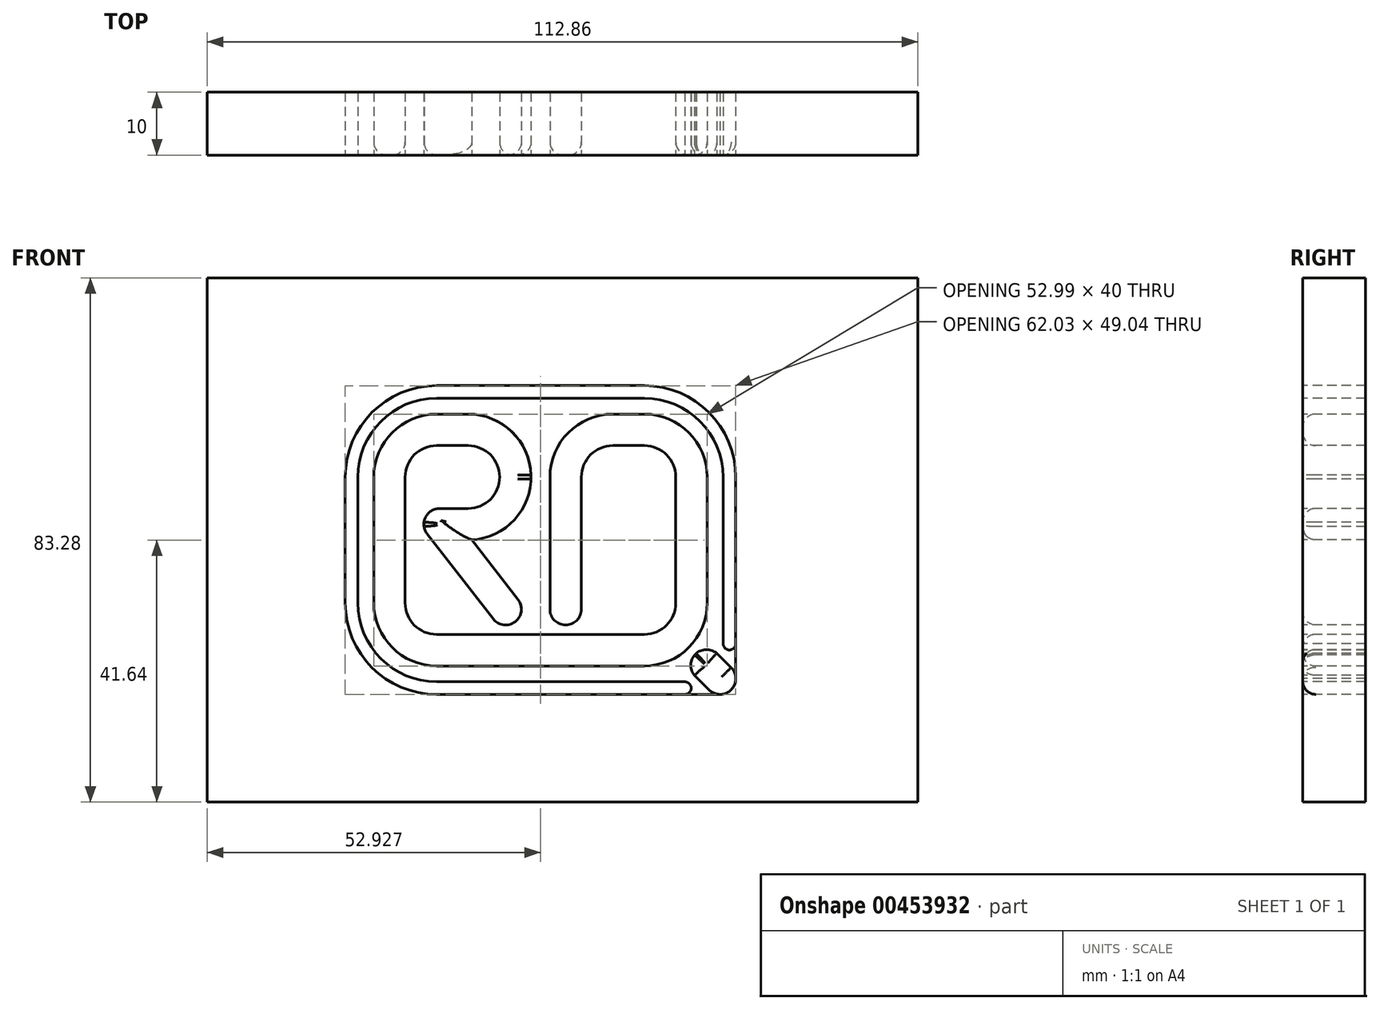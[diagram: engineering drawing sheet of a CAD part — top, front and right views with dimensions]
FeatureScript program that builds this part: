
annotation { "Feature Type Name" : "Feature", "Feature Type Description" : "" }
export const myFeature = defineFeature(function(context is Context, id is Id, definition is map)
    precondition{}
    {
        {
            var Q0;
            Q0=qCreatedBy(makeId("Front.planeOp"),FACE);
            var sketch = newSketch(context, id + "F0", { "sketchPlane" : qUnion([Q0])});
            skPoint(sketch, "E0.middle", {"position": v(0, 0) * mm});
            skLineSegment(sketch, "E1", {"start": v(-25, 10) * mm, "end": v(-25, -10) * mm});
            skLineSegment(sketch, "E2", {"start": v(-2, -20) * mm, "end": v(-0.38, -20) * mm});
            skLineSegment(sketch, "E3", {"start": v(-2, -11) * mm, "end": v(-2, 10) * mm});
            skLineSegment(sketch, "E4", {"start": v(8, 20) * mm, "end": v(13, 20) * mm});
            skLineSegment(sketch, "E5", {"start": v(23, 10) * mm, "end": v(23, -10) * mm});
            skLineSegment(sketch, "E6", {"start": v(13, -20) * mm, "end": v(9, -20) * mm});
            skLineSegment(sketch, "E7", {"start": v(-25, 20) * mm, "end": v(-15, 20) * mm});
            skLineSegment(sketch, "E8", {"start": v(-21, 0) * mm, "end": v(-15, 0) * mm, "construction": true});
            skLineSegment(sketch, "E9", {"start": v(-5, 10.33) * mm, "end": v(-5, 10.33) * mm});
            skPoint(sketch, "E10.visualSharp", {"position": v(-5.33, 20) * mm});
            skArc(sketch, "E10.filletArc", {"start": v(-5, 10.33) * mm, "mid": v(-8.05, 17.19) * mm, "end": v(-15, 20) * mm});
            skArc(sketch, "E11.filletArc", {"start": v(-15, 0) * mm, "mid": v(-7.81, 3.05) * mm, "end": v(-5, 10.33) * mm});
            skPoint(sketch, "E12.visualSharp", {"position": v(-3.63, -20) * mm});
            skPoint(sketch, "E13.visualSharp", {"position": v(23, -20) * mm});
            skArc(sketch, "E13.filletArc", {"start": v(13, -20) * mm, "mid": v(20.07, -17.07) * mm, "end": v(23, -10) * mm});
            skPoint(sketch, "E14.visualSharp", {"position": v(23, 20) * mm});
            skArc(sketch, "E14.filletArc", {"start": v(23, 10) * mm, "mid": v(20.07, 17.07) * mm, "end": v(13, 20) * mm});
            skPoint(sketch, "E15.visualSharp", {"position": v(-2, 20) * mm});
            skArc(sketch, "E15.filletArc", {"start": v(8, 20) * mm, "mid": v(0.92, 17.07) * mm, "end": v(-2, 10) * mm});
            skPoint(sketch, "E16.visualSharp", {"position": v(-2, -20) * mm});
            skArc(sketch, "E17.0", {"start": v(8, 15) * mm, "mid": v(4.46, 13.54) * mm, "end": v(3, 10) * mm});
            skLineSegment(sketch, "E17.1", {"start": v(3, -11) * mm, "end": v(3, 10) * mm});
            skLineSegment(sketch, "E17.2", {"start": v(8, 15) * mm, "end": v(13, 15) * mm});
            skArc(sketch, "E17.4", {"start": v(18, 10) * mm, "mid": v(16.53, 13.54) * mm, "end": v(13, 15) * mm});
            skLineSegment(sketch, "E17.5", {"start": v(18, 10) * mm, "end": v(18, -10) * mm});
            skArc(sketch, "E17.6", {"start": v(13, -15) * mm, "mid": v(16.53, -13.54) * mm, "end": v(18, -10) * mm});
            skLineSegment(sketch, "E17.7", {"start": v(13, -15) * mm, "end": v(9, -15) * mm});
            skArc(sketch, "E18.1", {"start": v(-15, 5) * mm, "mid": v(-11.44, 6.5) * mm, "end": v(-10, 10.08) * mm});
            skArc(sketch, "E18.2", {"start": v(-10, 10.08) * mm, "mid": v(-11.5, 13.56) * mm, "end": v(-15, 15) * mm});
            skLineSegment(sketch, "E18.3", {"start": v(-20, 15) * mm, "end": v(-15, 15) * mm});
            skLineSegment(sketch, "E19.0", {"start": v(-30, 17.5) * mm, "end": v(-30, -10) * mm});
            skLineSegment(sketch, "E20.0", {"start": v(-1, -15) * mm, "end": v(-0.38, -15) * mm});
            skLineSegment(sketch, "E21", {"start": v(-20, -20) * mm, "end": v(-2, -20) * mm});
            skLineSegment(sketch, "E22", {"start": v(-1, -15) * mm, "end": v(9, -15) * mm});
            skLineSegment(sketch, "E23.0", {"start": v(-20, -15) * mm, "end": v(0, -15) * mm});
            skLineSegment(sketch, "E24", {"start": v(-5, 10.33) * mm, "end": v(-5, 0) * mm});
            skLineSegment(sketch, "E25", {"start": v(0.5, -13.5) * mm, "end": v(0.5, -13.5) * mm});
            skPoint(sketch, "E26.visualSharp", {"position": v(3, -13.5) * mm});
            skArc(sketch, "E26.filletArc", {"start": v(0.5, -13.5) * mm, "mid": v(2.26, -12.77) * mm, "end": v(3, -11) * mm});
            skPoint(sketch, "E27.newPointB", {"position": v(-23.5, -13.5) * mm});
            skArc(sketch, "E27.filletArc", {"start": v(-2, -11) * mm, "mid": v(-1.27, -12.77) * mm, "end": v(0.5, -13.5) * mm});
            skPoint(sketch, "E28.visualSharp", {"position": v(-30, -20) * mm});
            skArc(sketch, "E28.filletArc", {"start": v(-30, -19.5) * mm, "mid": v(-29.85, -19.85) * mm, "end": v(-29.5, -20) * mm});
            skLineSegment(sketch, "E29", {"start": v(-7.28, -12.77) * mm, "end": v(-7.28, -12.77) * mm});
            skArc(sketch, "E30.filletArc", {"start": v(-7.28, -12.77) * mm, "mid": v(-6.55, -11) * mm, "end": v(-7.27, -9.24) * mm});
            skArc(sketch, "E31.filletArc", {"start": v(-11.23, -12.21) * mm, "mid": v(-9.4, -13.48) * mm, "end": v(-7.28, -12.77) * mm});
            skLineSegment(sketch, "E32.0", {"start": v(19.16, -19.7) * mm, "end": v(23.25, -23.79) * mm});
            skLineSegment(sketch, "E33.0", {"start": v(14.76, -15.3) * mm, "end": v(14.29, -14.83) * mm});
            skPoint(sketch, "E34.newPointB", {"position": v(-25, 20) * mm});
            skPoint(sketch, "E35.visualSharp", {"position": v(-23.5, 5) * mm});
            skPoint(sketch, "E36.visualSharp", {"position": v(-23.5, 0) * mm});
            skLineSegment(sketch, "E37", {"start": v(-30, 10) * mm, "end": v(-30, 17.5) * mm});
            skLineSegment(sketch, "E38", {"start": v(-20, 20) * mm, "end": v(-25, 20) * mm});
            skPoint(sketch, "E39.visualSharp", {"position": v(-30, 20) * mm});
            skArc(sketch, "E39.filletArc", {"start": v(-20, 20) * mm, "mid": v(-27.07, 17.07) * mm, "end": v(-30, 10) * mm});
            skArc(sketch, "E40", {"start": v(23.25, -23.79) * mm, "mid": v(26.79, -23.79) * mm, "end": v(26.78, -20.25) * mm});
            skPoint(sketch, "E41", {"position": v(20.07, -17.07) * mm});
            skPoint(sketch, "E42.orphan", {"position": v(16.53, -13.54) * mm});
            skLineSegment(sketch, "E43.trimOffspring", {"start": v(13, -20) * mm, "end": v(-0.38, -20) * mm});
            skArc(sketch, "E44.trimOffspring", {"start": v(19.16, -19.7) * mm, "mid": v(21.12, -18.14) * mm, "end": v(22.69, -16.19) * mm});
            skPoint(sketch, "E45.newPointB", {"position": v(-25, -20) * mm});
            skArc(sketch, "E45.filletArc", {"start": v(-25, -10) * mm, "mid": v(-23.54, -13.54) * mm, "end": v(-20, -15) * mm});
            skLineSegment(sketch, "E46", {"start": v(-15, 20) * mm, "end": v(8, 20) * mm});
            skLineSegment(sketch, "E47", {"start": v(21.86, -24.52) * mm, "end": v(-20, -24.52) * mm});
            skLineSegment(sketch, "E48", {"start": v(27.51, -22.02) * mm, "end": v(27.51, -18.87) * mm});
            skLineSegment(sketch, "E49", {"start": v(13, 24.52) * mm, "end": v(-20, 24.52) * mm});
            skLineSegment(sketch, "E50", {"start": v(-34.52, -10) * mm, "end": v(-34.52, 10) * mm});
            skPoint(sketch, "E51.orphan", {"position": v(17.43, -17.97) * mm});
            skPoint(sketch, "E52.orphan", {"position": v(13.35, -13.89) * mm});
            skArc(sketch, "E53.0", {"start": v(27.51, 10) * mm, "mid": v(23.26, 20.27) * mm, "end": v(13, 24.52) * mm});
            skArc(sketch, "E54.0", {"start": v(25.51, 10) * mm, "mid": v(21.85, 18.85) * mm, "end": v(13, 22.52) * mm});
            skLineSegment(sketch, "E55.0", {"start": v(25.51, -22.07) * mm, "end": v(25.51, -19) * mm});
            skLineSegment(sketch, "E56.0", {"start": v(25.02, -22.52) * mm, "end": v(21.98, -22.52) * mm});
            skLineSegment(sketch, "E57.0", {"start": v(-32.52, -10) * mm, "end": v(-32.52, 10) * mm});
            skLineSegment(sketch, "E58.0", {"start": v(13, 22.52) * mm, "end": v(-20, 22.52) * mm});
            skPoint(sketch, "E59.visualSharp", {"position": v(-32.52, 22.52) * mm});
            skArc(sketch, "E59.filletArc", {"start": v(-20, 22.52) * mm, "mid": v(-28.85, 18.85) * mm, "end": v(-32.52, 10) * mm});
            skArc(sketch, "E60.0", {"start": v(-20, 24.52) * mm, "mid": v(-30.27, 20.27) * mm, "end": v(-34.52, 10) * mm});
            skPoint(sketch, "E61.visualSharp", {"position": v(-32.52, -22.52) * mm});
            skLineSegment(sketch, "E62", {"start": v(26.51, -15) * mm, "end": v(26.51, -16.32) * mm});
            skLineSegment(sketch, "E63.0", {"start": v(18.1, -20.77) * mm, "end": v(22.19, -24.85) * mm, "construction": true});
            skLineSegment(sketch, "E64.0", {"start": v(23.75, -15.12) * mm, "end": v(27.84, -19.2) * mm, "construction": true});
            skArc(sketch, "E65", {"start": v(19.44, -24.52) * mm, "mid": v(20.44, -23.52) * mm, "end": v(19.44, -22.52) * mm});
            skArc(sketch, "E66", {"start": v(25.51, -16.47) * mm, "mid": v(26.51, -17.47) * mm, "end": v(27.51, -16.47) * mm});
            skLineSegment(sketch, "E67.trimOffspring", {"start": v(25.51, -14) * mm, "end": v(25.51, 10) * mm});
            skLineSegment(sketch, "E68.trimOffspring", {"start": v(27.51, -14) * mm, "end": v(27.51, 33) * mm});
            skLineSegment(sketch, "E69.trimOffspring", {"start": v(19.86, -22.52) * mm, "end": v(-20, -22.52) * mm});
            skLineSegment(sketch, "E70", {"start": v(21.86, -24.52) * mm, "end": v(25.02, -24.52) * mm});
            skLineSegment(sketch, "E71", {"start": v(27.51, -14) * mm, "end": v(27.51, -22.02) * mm});
            skLineSegment(sketch, "E72.bottom", {"start": v(-56.43, 41.64) * mm, "end": v(56.43, 41.64) * mm});
            skLineSegment(sketch, "E72.top", {"start": v(-56.43, -41.64) * mm, "end": v(56.43, -41.64) * mm});
            skLineSegment(sketch, "E72.left", {"start": v(-56.43, 41.64) * mm, "end": v(-56.43, -41.64) * mm});
            skLineSegment(sketch, "E72.right", {"start": v(56.43, 41.64) * mm, "end": v(56.43, -41.64) * mm});
            skLineSegment(sketch, "E73", {"start": v(0, 0) * mm, "end": v(0, -38.7) * mm, "construction": true});
            skLineSegment(sketch, "E74", {"start": v(0, 0) * mm, "end": v(33.56, 0) * mm, "construction": true});
            skArc(sketch, "E75.filletArc", {"start": v(-20, 15) * mm, "mid": v(-23.54, 13.54) * mm, "end": v(-25, 10) * mm});
            skArc(sketch, "E76.0", {"start": v(-30, -10) * mm, "mid": v(-27.07, -17.07) * mm, "end": v(-20, -20) * mm});
            skArc(sketch, "E77.0", {"start": v(-34.52, -10) * mm, "mid": v(-30.27, -20.27) * mm, "end": v(-20, -24.52) * mm});
            skArc(sketch, "E78.0", {"start": v(-32.52, -10) * mm, "mid": v(-28.85, -18.85) * mm, "end": v(-20, -22.52) * mm});
            skLineSegment(sketch, "E79", {"start": v(-15, 5) * mm, "end": v(-21, 5) * mm});
            skLineSegment(sketch, "E80", {"start": v(-23.5, 2.5) * mm, "end": v(-23.5, 2.5) * mm});
            skPoint(sketch, "E81.startSnap0", {"position": v(-6.55, -11) * mm});
            skArc(sketch, "E82.0", {"start": v(13, -22.52) * mm, "mid": v(21.85, -18.85) * mm, "end": v(25.51, -10) * mm});
            skArc(sketch, "E83", {"start": v(24.48, -17.98) * mm, "mid": v(21.11, -18.13) * mm, "end": v(20.96, -21.5) * mm});
            skLineSegment(sketch, "E84", {"start": v(24.48, -17.98) * mm, "end": v(26.78, -20.25) * mm});
            skLineSegment(sketch, "E85", {"start": v(25.51, -16.47) * mm, "end": v(25.51, -14) * mm});
            skLineSegment(sketch, "E86", {"start": v(-22, 7.18) * mm, "end": v(-22, -5.45) * mm});
            skArc(sketch, "E87", {"start": v(-19.53, 5) * mm, "mid": v(-22.03, 2.5) * mm, "end": v(-19.53, 0) * mm});
            skLineSegment(sketch, "E88", {"start": v(-21.5, 0.97) * mm, "end": v(-11.02, -12.53) * mm});
            skLineSegment(sketch, "E89.0", {"start": v(-17.54, 4.02) * mm, "end": v(-7.07, -9.47) * mm});
            skSolve(sketch);
        }
        {
            var Q0;
            Q0=makeQuery(id+"F0.imprint","IMPRINT",FACE,{"disambiguationData":[TD([[makeQuery(id+"F0.imprint","IMPRINT",EDGE,{"derivedFrom":sQuery(id+"F0.wireOp",EDGE,"E1")}),-1.0]])]});
            var Q1;
            {var subQ6=sQuery(id+"F0.wireOp",EDGE,"8dgEX87s-OnN3-UPAw-RyUf-tcfM0RuKeMZf");Q1=makeQuery(id+"F0.imprint","IMPRINT",FACE,{"disambiguationData":[TD([[makeQuery(id+"F0.imprint","IMPRINT",EDGE,{"derivedFrom":subQ6}),1.0]])]});}
            var Q2;
            {var subQ0=sQuery(id+"F0.wireOp",EDGE,"E40");var subQ1=makeQuery(id+"F0.imprint","INTERSECT",VERTEX,{"derivedFrom":[sQuery(id+"F0.wireOp",EDGE,"c0c087a9-fd36-4214-a694-875f0f01d769.0"),subQ0]});Q2=makeQuery(id+"F0.imprint","IMPRINT",FACE,{"disambiguationData":[TD([[makeQuery(id+"F0.imprint","IMPRINT",EDGE,{"disambiguationData":[TD([[subQ1,-1.0]])],"derivedFrom":subQ0}),1.0]])]});}
            var Q3;
            {var subQ0=sQuery(id+"F0.wireOp",EDGE,"E0.bottom");Q3=makeQuery(id+"F0.imprint","IMPRINT",FACE,{"disambiguationData":[TD([[makeQuery(id+"F0.imprint","IMPRINT",EDGE,{"derivedFrom":subQ0}),-1.0]])]});}
            var Q4;
            {var subQ0=sQuery(id+"F0.wireOp",EDGE,"E0.bottom");Q4=makeQuery(id+"F0.imprint","IMPRINT",FACE,{"disambiguationData":[TD([[makeQuery(id+"F0.imprint","IMPRINT",EDGE,{"derivedFrom":subQ0}),1.0]])]});}
            var Q5;
            {var subQ0=sQuery(id+"F0.wireOp",EDGE,"E31.filletArc");Q5=makeQuery(id+"F0.imprint","IMPRINT",FACE,{"disambiguationData":[TD([[makeQuery(id+"F0.imprint","IMPRINT",EDGE,{"derivedFrom":subQ0}),1.0]])]});}
            var Q6;
            {var subQ0=sQuery(id+"F0.wireOp",EDGE,"E83");var subQ1=sQuery(id+"F0.wireOp",EDGE,"E44.trimOffspring");var subQ2=makeQuery(id+"F0.imprint","INTERSECT",VERTEX,{"disambiguationData":[OD(0.0)],"derivedFrom":[subQ1,subQ0]});Q6=makeQuery(id+"F0.imprint","IMPRINT",FACE,{"disambiguationData":[TD([[makeQuery(id+"F0.imprint","IMPRINT",EDGE,{"disambiguationData":[TD([[subQ2,-1.0]])],"derivedFrom":subQ1}),-1.0]])]});}
            var Q7;
            {var subQ6=sQuery(id+"F0.wireOp",EDGE,"E32.0");var subQ8=makeQuery(id+"F0.imprint","IMPRINT",VERTEX,{"derivedFrom":subQ6});Q7=makeQuery(id+"F0.imprint","IMPRINT",FACE,{"disambiguationData":[TD([[makeQuery(id+"F0.imprint","IMPRINT",EDGE,{"disambiguationData":[TD([[subQ8,1.0]])],"derivedFrom":subQ6}),1.0]])]});}
            var Q8;
            {var subQ0=sQuery(id+"F0.wireOp",EDGE,"E83");var subQ1=sQuery(id+"F0.wireOp",EDGE,"E44.trimOffspring");var subQ2=makeQuery(id+"F0.imprint","INTERSECT",VERTEX,{"disambiguationData":[OD(0.0)],"derivedFrom":[subQ1,subQ0]});Q8=makeQuery(id+"F0.imprint","IMPRINT",FACE,{"disambiguationData":[TD([[makeQuery(id+"F0.imprint","IMPRINT",EDGE,{"disambiguationData":[TD([[subQ2,1.0]])],"derivedFrom":subQ1}),-1.0]])]});}
            extrude(context, id + "F1", {"entities" : qUnion([Q0, Q1, Q2, Q3, Q4, Q5, Q6, Q7, Q8]), "oppositeDirection" : true, "depth" : 10 * mm});
        }
        {
            var Q0;
            Q0=makeQuery(id+"F0.imprint","IMPRINT",FACE,{"disambiguationData":[TD([[makeQuery(id+"F0.imprint","IMPRINT",EDGE,{"derivedFrom":sQuery(id+"F0.wireOp",EDGE,"E49")}),1.0]])]});
            var Q1;
            {var subQ0=sQuery(id+"F0.wireOp",EDGE,"E65");var subQ2=makeQuery(id+"F0.imprint","IMPRINT",VERTEX,{"derivedFrom":subQ0});Q1=makeQuery(id+"F0.imprint","IMPRINT",FACE,{"disambiguationData":[TD([[makeQuery(id+"F0.imprint","IMPRINT",EDGE,{"disambiguationData":[TD([[subQ2,-1.0]])],"derivedFrom":subQ0}),1.0]])]});}
            var Q2;
            {var subQ0=sQuery(id+"F0.wireOp",EDGE,"E66");var subQ3=makeQuery(id+"F0.imprint","IMPRINT",VERTEX,{"derivedFrom":subQ0});Q2=makeQuery(id+"F0.imprint","IMPRINT",FACE,{"disambiguationData":[TD([[makeQuery(id+"F0.imprint","IMPRINT",EDGE,{"disambiguationData":[TD([[subQ3,1.0]])],"derivedFrom":subQ0}),1.0]])]});}
            extrude(context, id + "F2", {"entities" : qUnion([Q0, Q1, Q2]), "oppositeDirection" : true, "depth" : 10 * mm});
        }
        {
            var Q0;
            Q0=makeQuery(id+"F1.opExtrude","CAP_FACE",FACE,{"disambiguationData":[OSD([sQuery(id+"F0.wireOp",EDGE,"E1"),sQuery(id+"F0.wireOp",EDGE,"E2"),sQuery(id+"F0.wireOp",EDGE,"E3"),sQuery(id+"F0.wireOp",EDGE,"E4"),sQuery(id+"F0.wireOp",EDGE,"E5"),sQuery(id+"F0.wireOp",EDGE,"E7"),sQuery(id+"F0.wireOp",EDGE,"E10.filletArc"),sQuery(id+"F0.wireOp",EDGE,"E11.filletArc"),sQuery(id+"F0.wireOp",EDGE,"E13.filletArc"),sQuery(id+"F0.wireOp",EDGE,"E14.filletArc"),sQuery(id+"F0.wireOp",EDGE,"E15.filletArc"),sQuery(id+"F0.wireOp",EDGE,"E17.0"),sQuery(id+"F0.wireOp",EDGE,"E17.1"),sQuery(id+"F0.wireOp",EDGE,"E17.2"),sQuery(id+"F0.wireOp",EDGE,"E17.4"),sQuery(id+"F0.wireOp",EDGE,"E17.5"),sQuery(id+"F0.wireOp",EDGE,"E17.6"),sQuery(id+"F0.wireOp",EDGE,"E17.7"),sQuery(id+"F0.wireOp",EDGE,"E18.1"),sQuery(id+"F0.wireOp",EDGE,"E18.2"),sQuery(id+"F0.wireOp",EDGE,"E18.3"),sQuery(id+"F0.wireOp",EDGE,"E19.0"),sQuery(id+"F0.wireOp",EDGE,"E21"),sQuery(id+"F0.wireOp",EDGE,"E22"),sQuery(id+"F0.wireOp",EDGE,"E23.0"),sQuery(id+"F0.wireOp",EDGE,"E24"),sQuery(id+"F0.wireOp",EDGE,"E26.filletArc"),sQuery(id+"F0.wireOp",EDGE,"E27.filletArc"),sQuery(id+"F0.wireOp",EDGE,"E30.filletArc"),sQuery(id+"F0.wireOp",EDGE,"E31.filletArc"),sQuery(id+"F0.wireOp",EDGE,"E39.filletArc"),sQuery(id+"F0.wireOp",EDGE,"E43.trimOffspring"),sQuery(id+"F0.wireOp",EDGE,"E45.filletArc"),sQuery(id+"F0.wireOp",EDGE,"E75.filletArc"),sQuery(id+"F0.wireOp",EDGE,"E76.0"),sQuery(id+"F0.wireOp",EDGE,"E79"),sQuery(id+"F0.wireOp",EDGE,"E86"),sQuery(id+"F0.wireOp",EDGE,"E87"),sQuery(id+"F0.wireOp",EDGE,"E88"),sQuery(id+"F0.wireOp",EDGE,"E89.0")])],"isStart":true});
            var Q1;
            Q1=makeQuery(id+"F1.opExtrude","CAP_FACE",FACE,{"disambiguationData":[OSD([sQuery(id+"F0.wireOp",EDGE,"E32.0"),sQuery(id+"F0.wireOp",EDGE,"E40"),sQuery(id+"F0.wireOp",EDGE,"E44.trimOffspring"),sQuery(id+"F0.wireOp",EDGE,"E83"),sQuery(id+"F0.wireOp",EDGE,"E84")])],"isStart":true});
            fillet(context, id + "F3", {"entities" : qUnion([Q0, Q1]), "radius" : 2.1 * mm, "tangentPropagation" : true, "allowEdgeOverflow" : false});
        }
        {
            var Q0;
            Q0=makeQuery(id+"F0.imprint","IMPRINT",FACE,{"disambiguationData":[TD([[makeQuery(id+"F0.imprint","IMPRINT",EDGE,{"derivedFrom":sQuery(id+"F0.wireOp",EDGE,"E1")}),1.0]])]});
            var Q1;
            {var subQ16=sQuery(id+"F0.wireOp",EDGE,"E2");Q1=makeQuery(id+"F0.imprint","IMPRINT",FACE,{"disambiguationData":[TD([[makeQuery(id+"F0.imprint","IMPRINT",EDGE,{"derivedFrom":subQ16}),-1.0]])]});}
            var Q2;
            {var subQ10=sQuery(id+"F0.wireOp",EDGE,"E65");Q2=makeQuery(id+"F0.imprint","IMPRINT",FACE,{"disambiguationData":[TD([[makeQuery(id+"F0.imprint","IMPRINT",EDGE,{"derivedFrom":subQ10}),-1.0]])]});}
            var Q3;
            {var subQ0=sQuery(id+"F0.wireOp",EDGE,"E44.trimOffspring");var subQ1=sQuery(id+"F0.wireOp",EDGE,"E32.0");var subQ2=makeQuery(id+"F0.imprint","INTERSECT",VERTEX,{"derivedFrom":[subQ1,subQ0]});Q3=makeQuery(id+"F0.imprint","IMPRINT",FACE,{"disambiguationData":[TD([[makeQuery(id+"F0.imprint","IMPRINT",EDGE,{"disambiguationData":[TD([[subQ2,-1.0]])],"derivedFrom":subQ1}),1.0]])]});}
            var Q4;
            {var subQ0=sQuery(id+"F0.wireOp",EDGE,"E83");var subQ1=sQuery(id+"F0.wireOp",EDGE,"E32.0");var subQ2=makeQuery(id+"F0.imprint","INTERSECT",VERTEX,{"derivedFrom":[subQ1,subQ0]});Q4=makeQuery(id+"F0.imprint","IMPRINT",FACE,{"disambiguationData":[TD([[makeQuery(id+"F0.imprint","IMPRINT",EDGE,{"disambiguationData":[TD([[subQ2,1.0]])],"derivedFrom":subQ1}),1.0]])]});}
            var Q5;
            {var subQ1=sQuery(id+"F0.wireOp",EDGE,"E66");Q5=makeQuery(id+"F0.imprint","IMPRINT",FACE,{"disambiguationData":[TD([[makeQuery(id+"F0.imprint","IMPRINT",EDGE,{"derivedFrom":subQ1}),-1.0]])]});}
            extrude(context, id + "F4", {"entities" : qUnion([Q0, Q1, Q2, Q3, Q4, Q5]), "oppositeDirection" : true, "depth" : 10 * mm});
        }
        {
            var Q0;
            Q0=makeQuery(id+"F0.imprint","IMPRINT",FACE,{"disambiguationData":[TD([[makeQuery(id+"F0.imprint","IMPRINT",EDGE,{"derivedFrom":sQuery(id+"F0.wireOp",EDGE,"E49")}),-1.0]])]});
            extrude(context, id + "F5", {"entities" : qUnion([Q0]), "oppositeDirection" : true, "depth" : 10 * mm});
        }
    });
